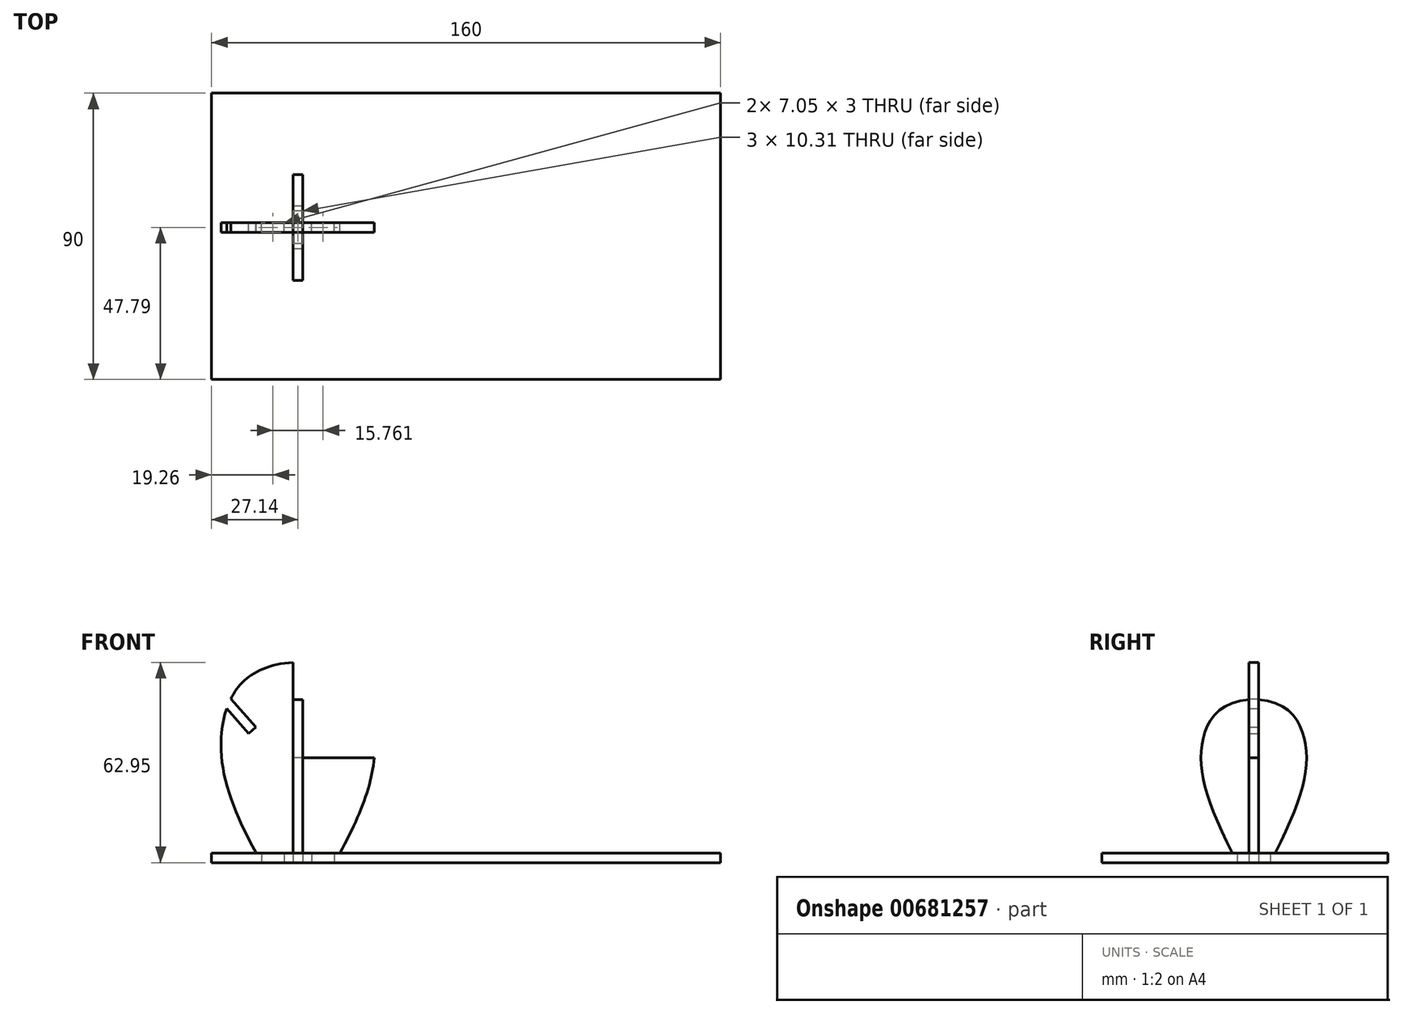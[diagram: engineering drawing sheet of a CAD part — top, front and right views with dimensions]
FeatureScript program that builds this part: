
annotation { "Feature Type Name" : "Feature", "Feature Type Description" : "" }
export const myFeature = defineFeature(function(context is Context, id is Id, definition is map)
    precondition{}
    {
        {
            assignVariable(context, id + "F0", {"name" : "MaterialDepth", "anyValue" : 3 * mm});
        }
        {
            var Q0;
            Q0=qCreatedBy(makeId("Front.planeOp"),FACE);
            var sketch = newSketch(context, id + "F1", { "sketchPlane" : qUnion([Q0])});
            skFitSpline(sketch, "E0", {"points": [v(0, 60) * mm, v(-24, 37.8) * mm, v(-13.13, 0) * mm], "startDerivative": vector(-111.27, -1.94) * mm, "endDerivative": vector(45.33, -82.54) * mm});
            skFitSpline(sketch, "E1.MirrorCS", {"points": [v(0, 60) * mm, v(24, 37.8) * mm, v(13.13, 0) * mm], "startDerivative": vector(111.27, -1.94) * mm, "endDerivative": vector(-45.33, -82.54) * mm});
            skLineSegment(sketch, "E2", {"start": v(-13.13, 0) * mm, "end": v(-11.4, 0) * mm});
            skLineSegment(sketch, "E3.bottom", {"start": v(-4.35, -3) * mm, "end": v(-11.4, -3) * mm});
            skLineSegment(sketch, "E3.left", {"start": v(-4.35, -3) * mm, "end": v(-4.35, 0) * mm});
            skLineSegment(sketch, "E3.right", {"start": v(-11.4, -3) * mm, "end": v(-11.4, 0) * mm});
            skLineSegment(sketch, "E4.trimOffspring", {"start": v(-4.35, 0) * mm, "end": v(-1.38, 0) * mm});
            skLineSegment(sketch, "E5.MirrorCS", {"start": v(4.35, -3) * mm, "end": v(4.35, 0) * mm});
            skLineSegment(sketch, "E6.MirrorCS", {"start": v(4.35, -3) * mm, "end": v(11.4, -3) * mm});
            skLineSegment(sketch, "E7.MirrorCS", {"start": v(11.4, -3) * mm, "end": v(11.4, 0) * mm});
            skLineSegment(sketch, "E8.trimOffspring", {"start": v(11.4, 0) * mm, "end": v(13.13, 0) * mm});
            skLineSegment(sketch, "E9.trimOffspring", {"start": v(1.62, 0) * mm, "end": v(4.35, 0) * mm});
            skLineSegment(sketch, "E10", {"start": v(1.62, 0) * mm, "end": v(-1.38, 0) * mm});
            skLineSegment(sketch, "E11", {"start": v(0, 60) * mm, "end": v(0, -7.3) * mm, "construction": true});
            skSolve(sketch);
        }
        {
            var Q0;
            Q0=makeQuery(id+"F1.imprint","IMPRINT",FACE,{"disambiguationData":[TD([[makeQuery(id+"F1.imprint","IMPRINT",EDGE,{"derivedFrom":sQuery(id+"F1.wireOp",EDGE,"E0")}),1.0]])]});
            extrude(context, id + "F2", {"entities" : qUnion([Q0]), "endBound" : BoundingType.SYMMETRIC, "depth" : getVariable(context, 'MaterialDepth'), "offsetDistance" : 25 * mm});
        }
        {
            var Q0;
            Q0=qCreatedBy(makeId("Front.planeOp"),FACE);
            var sketch = newSketch(context, id + "F3", { "sketchPlane" : qUnion([Q0])});
            skPoint(sketch, "E12", {"position": v(-21.83, 47.04) * mm});
            skLineSegment(sketch, "E13", {"start": v(-21.83, 47.04) * mm, "end": v(-18.44, 43.18) * mm, "construction": true});
            skLineSegment(sketch, "E14", {"start": v(-24.6, 44.62) * mm, "end": v(-21.83, 47.04) * mm, "construction": true});
            skLineSegment(sketch, "E15", {"start": v(-30.36, 54.52) * mm, "end": v(-29.23, 55.5) * mm});
            skLineSegment(sketch, "E16.MirrorCS", {"start": v(-15.55, 37.6) * mm, "end": v(-14.42, 38.58) * mm});
            skLineSegment(sketch, "E17", {"start": v(-30.36, 54.52) * mm, "end": v(-15.55, 37.6) * mm});
            skLineSegment(sketch, "E18.MirrorCS", {"start": v(-28.1, 56.5) * mm, "end": v(-29.23, 55.5) * mm});
            skLineSegment(sketch, "E19.MirrorCS", {"start": v(-28.1, 56.5) * mm, "end": v(-13.3, 39.57) * mm});
            skLineSegment(sketch, "E20.MirrorCS", {"start": v(-13.3, 39.57) * mm, "end": v(-14.42, 38.58) * mm});
            skPoint(sketch, "E21", {"position": v(11.66, 57.67) * mm});
            skLineSegment(sketch, "E22", {"start": v(11.66, 57.67) * mm, "end": v(8.66, 47.36) * mm, "construction": true});
            skLineSegment(sketch, "E23", {"start": v(11.66, 57.67) * mm, "end": v(16.96, 56.12) * mm, "construction": true});
            skLineSegment(sketch, "E24", {"start": v(10.77, 49.25) * mm, "end": v(9.33, 49.67) * mm});
            skLineSegment(sketch, "E25.MirrorCS", {"start": v(15.43, 65.25) * mm, "end": v(14, 65.67) * mm});
            skLineSegment(sketch, "E26", {"start": v(10.77, 49.25) * mm, "end": v(15.43, 65.25) * mm});
            skLineSegment(sketch, "E27.MirrorCS", {"start": v(7.89, 50.09) * mm, "end": v(9.33, 49.67) * mm});
            skLineSegment(sketch, "E28.MirrorCS", {"start": v(7.89, 50.09) * mm, "end": v(12.55, 66.09) * mm});
            skLineSegment(sketch, "E29.MirrorCS", {"start": v(12.55, 66.09) * mm, "end": v(14, 65.67) * mm});
            skPoint(sketch, "E30", {"position": v(22.55, 45.1) * mm});
            skLineSegment(sketch, "E31", {"start": v(33.64, 54.63) * mm, "end": v(22.55, 45.1) * mm, "construction": true});
            skLineSegment(sketch, "E32", {"start": v(22.55, 45.1) * mm, "end": v(32, 34.1) * mm, "construction": true});
            skLineSegment(sketch, "E33", {"start": v(33, 52.11) * mm, "end": v(32.03, 53.25) * mm});
            skLineSegment(sketch, "E34.MirrorCS", {"start": v(14.04, 35.82) * mm, "end": v(13.06, 36.96) * mm});
            skLineSegment(sketch, "E35", {"start": v(14.04, 35.82) * mm, "end": v(33, 52.11) * mm});
            skLineSegment(sketch, "E36.MirrorCS", {"start": v(12.09, 38.1) * mm, "end": v(31.05, 54.39) * mm});
            skLineSegment(sketch, "E37.MirrorCS", {"start": v(31.05, 54.39) * mm, "end": v(32.03, 53.25) * mm});
            skLineSegment(sketch, "E38.MirrorCS", {"start": v(12.09, 38.1) * mm, "end": v(13.06, 36.96) * mm});
            skLineSegment(sketch, "E39.bottom", {"start": v(1.5, -30) * mm, "end": v(-1.5, -30) * mm});
            skLineSegment(sketch, "E39.top", {"start": v(1.5, 30) * mm, "end": v(-1.5, 30) * mm});
            skLineSegment(sketch, "E39.left", {"start": v(1.5, -30) * mm, "end": v(1.5, 30) * mm});
            skLineSegment(sketch, "E39.right", {"start": v(-1.5, -30) * mm, "end": v(-1.5, 30) * mm});
            skPoint(sketch, "E39.middle", {"position": v(0, 0) * mm});
            skSolve(sketch);
        }
        {
            var Q0;
            Q0 = qSketchRegion(id + "F3", true);
            extrude(context, id + "F4", {"entities" : qUnion([Q0]), "operationType" : NewBodyOperationType.REMOVE, "endBound" : BoundingType.SYMMETRIC, "depth" : 25 * mm, "offsetDistance" : 25 * mm});
        }
        {
            var Q0;
            Q0=qCreatedBy(makeId("Right.planeOp"),FACE);
            var sketch = newSketch(context, id + "F5", { "sketchPlane" : qUnion([Q0])});
            skFitSpline(sketch, "E40", {"points": [v(0, 48.26) * mm, v(-16.18, 34.7) * mm, v(-6.76, 0) * mm], "startDerivative": vector(-76.37, -0.67) * mm, "endDerivative": vector(42.97, -85.49) * mm});
            skFitSpline(sketch, "E41.MirrorCS", {"points": [v(0, 48.26) * mm, v(16.18, 34.7) * mm, v(6.76, 0) * mm], "startDerivative": vector(76.37, -0.67) * mm, "endDerivative": vector(-42.97, -85.49) * mm});
            skLineSegment(sketch, "E42", {"start": v(-6.76, 0) * mm, "end": v(-5.16, 0) * mm});
            skPoint(sketch, "E43.middle", {"position": v(0, 36.6) * mm});
            skLineSegment(sketch, "E44.bottom", {"start": v(5.16, -3) * mm, "end": v(-5.16, -3) * mm});
            skLineSegment(sketch, "E44.left", {"start": v(5.16, -3) * mm, "end": v(5.16, 0) * mm});
            skLineSegment(sketch, "E44.right", {"start": v(-5.16, -3) * mm, "end": v(-5.16, 0) * mm});
            skPoint(sketch, "E44.middle", {"position": v(0, 0) * mm});
            skLineSegment(sketch, "E45.trimOffspring", {"start": v(5.16, 0) * mm, "end": v(6.76, 0) * mm});
            skSolve(sketch);
        }
        {
            var Q0;
            Q0 = qSketchRegion(id + "F5", true);
            extrude(context, id + "F6", {"entities" : qUnion([Q0]), "endBound" : BoundingType.SYMMETRIC, "depth" : getVariable(context, 'MaterialDepth'), "offsetDistance" : 25 * mm});
        }
        {
            var Q0;
            Q0=makeQuery(id+"F6.opExtrude","CAP_FACE",FACE,{"disambiguationData":[OSD([sQuery(id+"F5.wireOp",EDGE,"E40"),sQuery(id+"F5.wireOp",EDGE,"E41.MirrorCS"),sQuery(id+"F5.wireOp",EDGE,"E42"),sQuery(id+"F5.wireOp",EDGE,"E44.bottom"),sQuery(id+"F5.wireOp",EDGE,"E44.left"),sQuery(id+"F5.wireOp",EDGE,"E44.right"),sQuery(id+"F5.wireOp",EDGE,"E45.trimOffspring")])],"isStart":true});
            var sketch = newSketch(context, id + "F7", { "sketchPlane" : qUnion([Q0])});
            skLineSegment(sketch, "E46.bottom", {"start": v(1.5, 148.9) * mm, "end": v(-1.5, 148.9) * mm});
            skLineSegment(sketch, "E46.top", {"start": v(1.5, 30) * mm, "end": v(-1.5, 30) * mm});
            skLineSegment(sketch, "E46.left", {"start": v(1.5, 148.9) * mm, "end": v(1.5, 30) * mm});
            skLineSegment(sketch, "E46.right", {"start": v(-1.5, 148.9) * mm, "end": v(-1.5, 30) * mm});
            skPoint(sketch, "E46.middle", {"position": v(0, 89.45) * mm});
            skSolve(sketch);
        }
        {
            var Q0;
            Q0 = qSketchRegion(id + "F7", true);
            extrude(context, id + "F8", {"entities" : qUnion([Q0]), "operationType" : NewBodyOperationType.REMOVE, "endBound" : BoundingType.THROUGH_ALL, "oppositeDirection" : true, "depth" : getVariable(context, 'MaterialDepth'), "offsetDistance" : 25 * mm});
        }
        {
            var Q0;
            Q0=makeQuery(id+"F2.opExtrude","SWEPT_FACE",FACE,{"disambiguationData":[OSD([sQuery(id+"F1.wireOp",EDGE,"E6.MirrorCS")])]});
            var sketch = newSketch(context, id + "F9", { "sketchPlane" : qUnion([Q0])});
            skLineSegment(sketch, "E47.bottom", {"start": v(132.86, -42.21) * mm, "end": v(-27.14, -42.21) * mm});
            skLineSegment(sketch, "E47.top", {"start": v(132.86, 47.79) * mm, "end": v(-27.14, 47.79) * mm});
            skLineSegment(sketch, "E47.left", {"start": v(132.86, -42.21) * mm, "end": v(132.86, 47.79) * mm});
            skLineSegment(sketch, "E47.right", {"start": v(-27.14, -42.21) * mm, "end": v(-27.14, 47.79) * mm});
            skLineSegment(sketch, "E48.0", {"start": v(4.35, -1.5) * mm, "end": v(11.4, -1.5) * mm});
            skLineSegment(sketch, "E48.1", {"start": v(11.4, 1.5) * mm, "end": v(11.4, -1.5) * mm});
            skLineSegment(sketch, "E48.2", {"start": v(4.35, 1.5) * mm, "end": v(11.4, 1.5) * mm});
            skLineSegment(sketch, "E48.3", {"start": v(4.35, 1.5) * mm, "end": v(4.35, -1.5) * mm});
            skLineSegment(sketch, "E48.4", {"start": v(-4.35, 1.5) * mm, "end": v(-4.35, -1.5) * mm});
            skLineSegment(sketch, "E48.5", {"start": v(-11.4, 1.5) * mm, "end": v(-11.4, -1.5) * mm});
            skLineSegment(sketch, "E48.6", {"start": v(-4.35, -1.5) * mm, "end": v(-11.4, -1.5) * mm});
            skLineSegment(sketch, "E48.7", {"start": v(-4.35, 1.5) * mm, "end": v(-11.4, 1.5) * mm});
            skLineSegment(sketch, "E48.8", {"start": v(-1.5, -5.16) * mm, "end": v(-1.5, 5.16) * mm});
            skLineSegment(sketch, "E48.9", {"start": v(1.5, 5.16) * mm, "end": v(-1.5, 5.16) * mm});
            skLineSegment(sketch, "E48.10", {"start": v(1.5, -5.16) * mm, "end": v(1.5, 5.16) * mm});
            skLineSegment(sketch, "E48.11", {"start": v(1.5, -5.16) * mm, "end": v(-1.5, -5.16) * mm});
            skSolve(sketch);
        }
        {
            var Q0;
            Q0 = qSketchRegion(id + "F9", true);
            extrude(context, id + "F10", {"entities" : qUnion([Q0]), "oppositeDirection" : true, "depth" : getVariable(context, 'MaterialDepth'), "offsetDistance" : 25 * mm});
        }
    });
